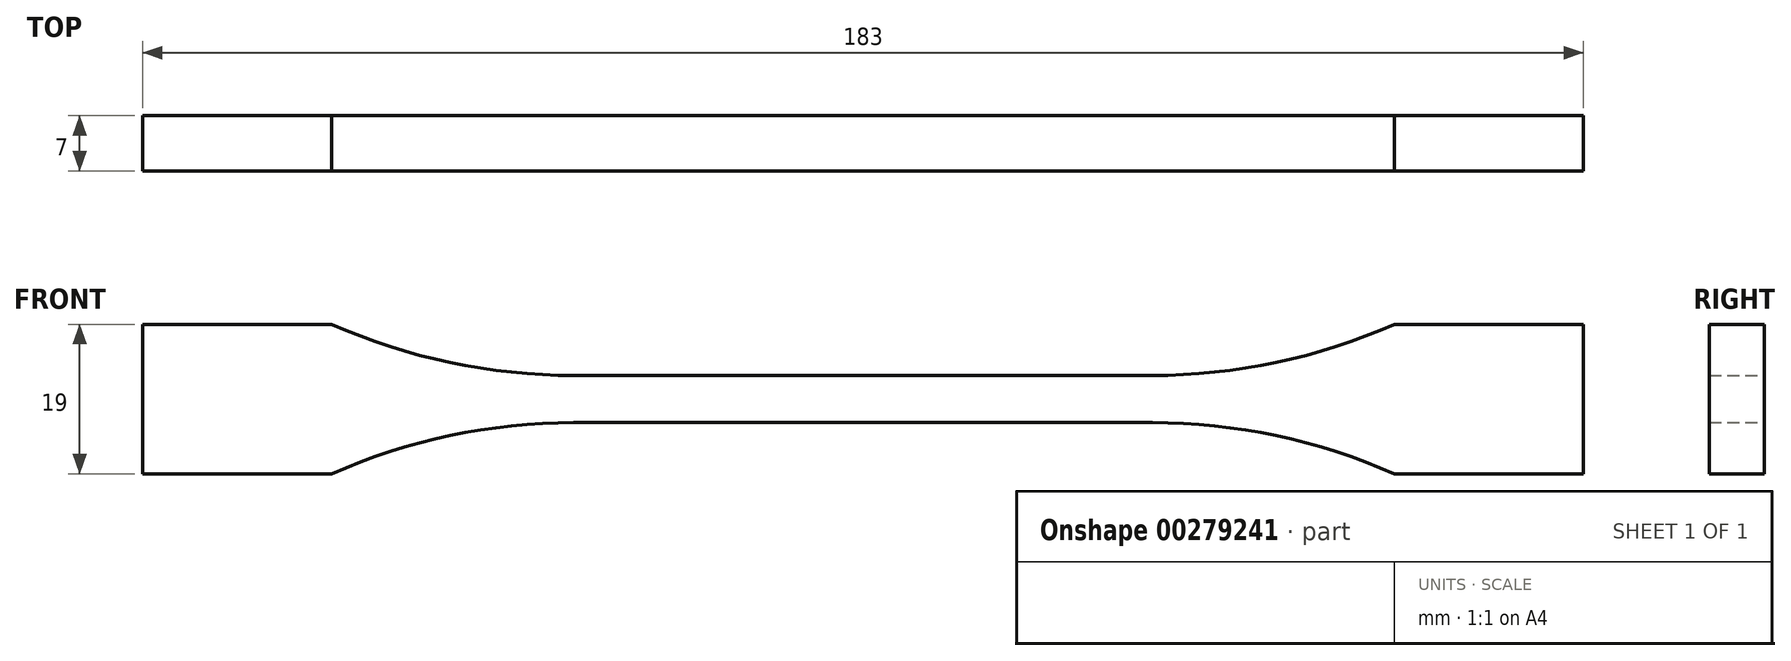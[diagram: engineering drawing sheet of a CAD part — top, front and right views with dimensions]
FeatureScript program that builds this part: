
annotation { "Feature Type Name" : "Feature", "Feature Type Description" : "" }
export const myFeature = defineFeature(function(context is Context, id is Id, definition is map)
    precondition{}
    {
        {
            var Q0;
            Q0=qCreatedBy(makeId("Front.planeOp"),FACE);
            var sketch = newSketch(context, id + "F0", { "sketchPlane" : qUnion([Q0])});
            skLineSegment(sketch, "E0", {"start": v(0, 3) * mm, "end": v(36.75, 3) * mm});
            skArc(sketch, "E1", {"start": v(36.75, 3) * mm, "mid": v(52.46, 4.64) * mm, "end": v(67.5, 9.5) * mm});
            skLineSegment(sketch, "E2", {"start": v(67.5, 9.5) * mm, "end": v(91.5, 9.5) * mm});
            skLineSegment(sketch, "E3.MirrorCS", {"start": v(0, -3) * mm, "end": v(36.75, -3) * mm});
            skLineSegment(sketch, "E4.MirrorCS", {"start": v(67.5, -9.5) * mm, "end": v(91.5, -9.5) * mm});
            skArc(sketch, "E5.MirrorCS", {"start": v(36.75, -3) * mm, "mid": v(52.46, -4.64) * mm, "end": v(67.5, -9.5) * mm});
            skLineSegment(sketch, "E6.MirrorCS", {"start": v(0, 3) * mm, "end": v(-36.75, 3) * mm});
            skArc(sketch, "E7.MirrorCS", {"start": v(-36.75, 3) * mm, "mid": v(-52.46, 4.64) * mm, "end": v(-67.5, 9.5) * mm});
            skLineSegment(sketch, "E8.MirrorCS", {"start": v(-67.5, 9.5) * mm, "end": v(-91.5, 9.5) * mm});
            skLineSegment(sketch, "E9.MirrorCS", {"start": v(0, -3) * mm, "end": v(-36.75, -3) * mm});
            skArc(sketch, "E10.MirrorCS", {"start": v(-36.75, -3) * mm, "mid": v(-52.46, -4.64) * mm, "end": v(-67.5, -9.5) * mm});
            skLineSegment(sketch, "E11.MirrorCS", {"start": v(-67.5, -9.5) * mm, "end": v(-91.5, -9.5) * mm});
            skLineSegment(sketch, "E12", {"start": v(91.5, 9.5) * mm, "end": v(91.5, -9.5) * mm});
            skLineSegment(sketch, "E13", {"start": v(-91.5, 9.5) * mm, "end": v(-91.5, -9.5) * mm});
            skSolve(sketch);
        }
        {
            var Q0;
            Q0 = qSketchRegion(id + "F0", true);
            extrude(context, id + "F1", {"entities" : qUnion([Q0]), "endBound" : BoundingType.SYMMETRIC, "depth" : 7 * mm});
        }
    });
